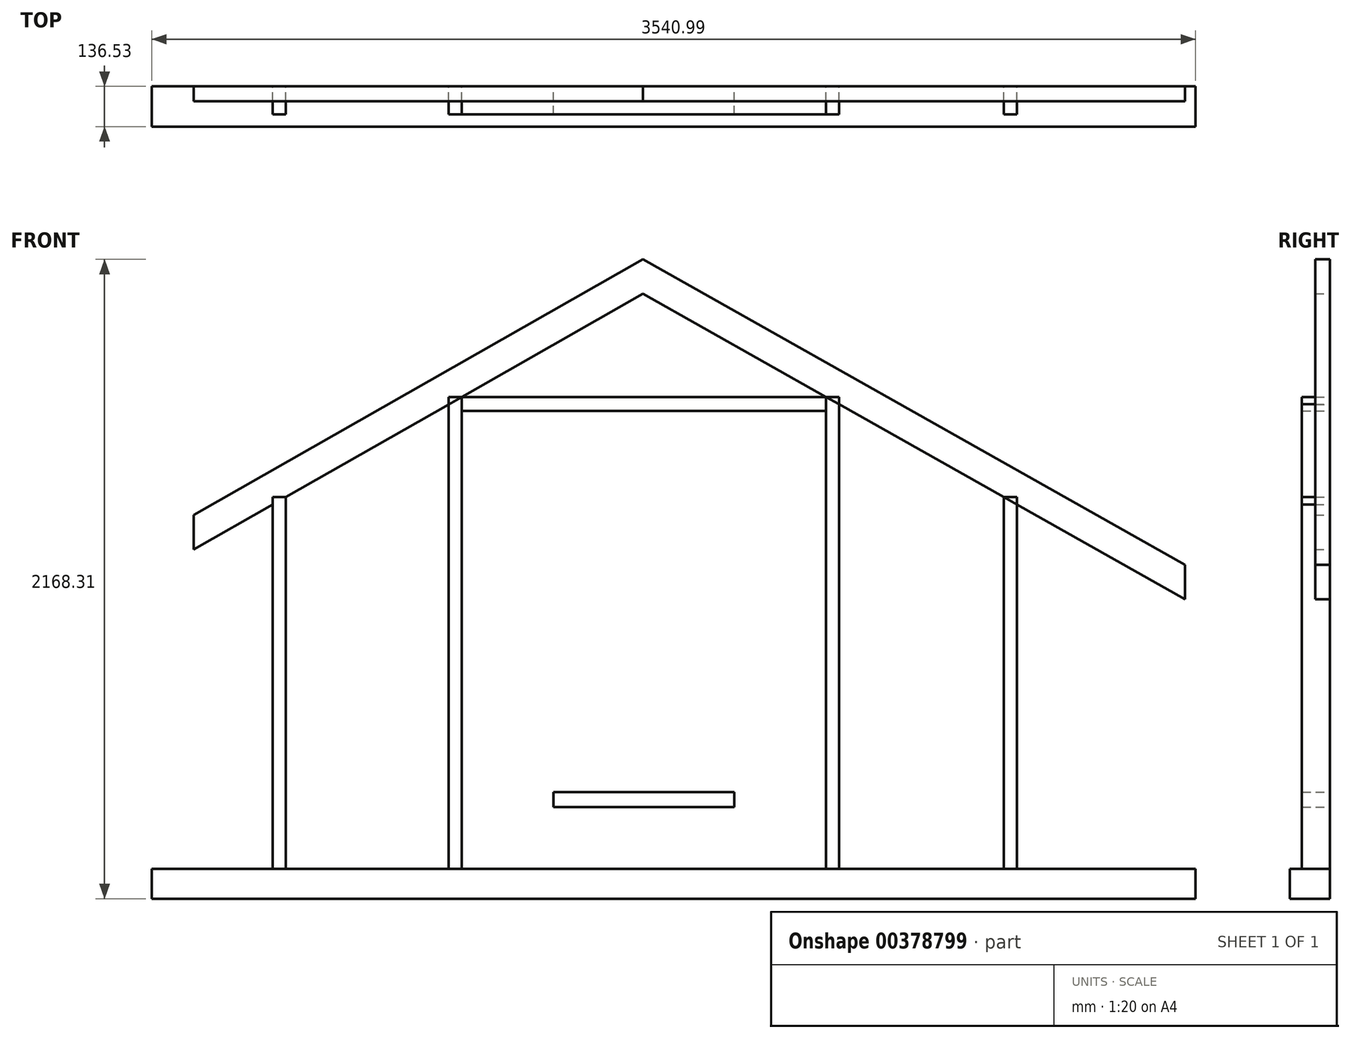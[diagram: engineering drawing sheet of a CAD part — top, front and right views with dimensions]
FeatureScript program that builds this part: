
annotation { "Feature Type Name" : "Feature", "Feature Type Description" : "" }
export const myFeature = defineFeature(function(context is Context, id is Id, definition is map)
    precondition{}
    {
        {
            var Q0;
            Q0=qCreatedBy(makeId("Front.planeOp"),FACE);
            var sketch = newSketch(context, id + "F0", { "sketchPlane" : qUnion([Q0])});
            skLineSegment(sketch, "E0.bottom", {"start": v(-586.63, -18.31) * mm, "end": v(648.44, -18.31) * mm});
            skLineSegment(sketch, "E0.top", {"start": v(-586.63, -65.94) * mm, "end": v(648.44, -65.94) * mm});
            skLineSegment(sketch, "E0.left", {"start": v(-586.63, -18.31) * mm, "end": v(-586.63, -65.94) * mm});
            skLineSegment(sketch, "E0.right", {"start": v(648.44, -18.31) * mm, "end": v(648.44, -65.94) * mm});
            skLineSegment(sketch, "E1.bottom", {"start": v(648.44, -18.31) * mm, "end": v(692.9, -18.31) * mm});
            skLineSegment(sketch, "E1.top", {"start": v(648.44, -1618.51) * mm, "end": v(692.9, -1618.51) * mm});
            skLineSegment(sketch, "E1.left", {"start": v(648.44, -18.31) * mm, "end": v(648.44, -1618.51) * mm});
            skLineSegment(sketch, "E1.right", {"start": v(692.9, -18.31) * mm, "end": v(692.9, -1618.51) * mm});
            skLineSegment(sketch, "E2.bottom", {"start": v(337.3, -65.94) * mm, "end": v(381.74, -65.94) * mm});
            skLineSegment(sketch, "E2.top", {"start": v(337.3, -1618.51) * mm, "end": v(381.74, -1618.51) * mm});
            skLineSegment(sketch, "E2.left", {"start": v(337.3, -65.94) * mm, "end": v(337.3, -1618.51) * mm});
            skLineSegment(sketch, "E2.right", {"start": v(381.74, -65.94) * mm, "end": v(381.74, -1618.51) * mm});
            skLineSegment(sketch, "E3.bottom", {"start": v(1251.7, -358.04) * mm, "end": v(1296.14, -358.04) * mm});
            skLineSegment(sketch, "E3.top", {"start": v(1251.7, -1618.51) * mm, "end": v(1296.14, -1618.51) * mm});
            skLineSegment(sketch, "E3.left", {"start": v(1251.7, -358.04) * mm, "end": v(1251.7, -1618.51) * mm});
            skLineSegment(sketch, "E3.right", {"start": v(1296.14, -358.04) * mm, "end": v(1296.14, -1618.51) * mm});
            skLineSegment(sketch, "E4", {"start": v(1251.7, -358.04) * mm, "end": v(648.44, -18.31) * mm});
            skLineSegment(sketch, "E5", {"start": v(648.44, -18.31) * mm, "end": v(27.64, 331.3) * mm});
            skLineSegment(sketch, "E6.bottom", {"start": v(-586.63, -18.31) * mm, "end": v(-631.08, -18.31) * mm});
            skLineSegment(sketch, "E6.top", {"start": v(-586.63, -1618.51) * mm, "end": v(-631.08, -1618.51) * mm});
            skLineSegment(sketch, "E6.left", {"start": v(-586.63, -18.31) * mm, "end": v(-586.63, -1618.51) * mm});
            skLineSegment(sketch, "E6.right", {"start": v(-631.08, -18.31) * mm, "end": v(-631.08, -1618.51) * mm});
            skLineSegment(sketch, "E7.bottom", {"start": v(-319.93, -65.94) * mm, "end": v(-275.48, -65.94) * mm});
            skLineSegment(sketch, "E7.top", {"start": v(-319.93, -1618.51) * mm, "end": v(-275.48, -1618.51) * mm});
            skLineSegment(sketch, "E7.left", {"start": v(-319.93, -65.94) * mm, "end": v(-319.93, -1618.51) * mm});
            skLineSegment(sketch, "E7.right", {"start": v(-275.48, -65.94) * mm, "end": v(-275.48, -1618.51) * mm});
            skLineSegment(sketch, "E8.bottom", {"start": v(-1227.98, -358.04) * mm, "end": v(-1183.53, -358.04) * mm});
            skLineSegment(sketch, "E8.top", {"start": v(-1227.98, -1618.51) * mm, "end": v(-1183.53, -1618.51) * mm});
            skLineSegment(sketch, "E8.left", {"start": v(-1227.98, -358.04) * mm, "end": v(-1227.98, -1618.51) * mm});
            skLineSegment(sketch, "E8.right", {"start": v(-1183.53, -358.04) * mm, "end": v(-1183.53, -1618.51) * mm});
            skLineSegment(sketch, "E9", {"start": v(-1183.53, -358.04) * mm, "end": v(-586.63, -18.31) * mm});
            skLineSegment(sketch, "E10", {"start": v(-586.63, -18.31) * mm, "end": v(27.64, 331.3) * mm});
            skLineSegment(sketch, "E11.bottom", {"start": v(-275.48, -1358.16) * mm, "end": v(337.3, -1358.16) * mm});
            skLineSegment(sketch, "E11.top", {"start": v(-275.48, -1408.96) * mm, "end": v(337.3, -1408.96) * mm});
            skLineSegment(sketch, "E11.left", {"start": v(-275.48, -1358.16) * mm, "end": v(-275.48, -1408.96) * mm});
            skLineSegment(sketch, "E11.right", {"start": v(337.3, -1358.16) * mm, "end": v(337.3, -1408.96) * mm});
            skLineSegment(sketch, "E12", {"start": v(27.64, 331.3) * mm, "end": v(27.64, 448.2) * mm});
            skLineSegment(sketch, "E13", {"start": v(27.64, 448.2) * mm, "end": v(-1496.57, -419.3) * mm});
            skLineSegment(sketch, "E14", {"start": v(-1496.57, -419.3) * mm, "end": v(-1496.57, -536.2) * mm});
            skLineSegment(sketch, "E15", {"start": v(-1496.57, -536.2) * mm, "end": v(-1183.53, -358.04) * mm});
            skLineSegment(sketch, "E16", {"start": v(27.64, 448.2) * mm, "end": v(1866.28, -587.24) * mm});
            skLineSegment(sketch, "E17", {"start": v(1866.28, -587.24) * mm, "end": v(1866.28, -704.15) * mm});
            skLineSegment(sketch, "E18", {"start": v(1866.28, -704.15) * mm, "end": v(1251.7, -358.04) * mm});
            skLineSegment(sketch, "E19.bottom", {"start": v(-1638.65, -1618.51) * mm, "end": v(1902.34, -1618.51) * mm});
            skLineSegment(sketch, "E19.top", {"start": v(-1638.65, -1720.11) * mm, "end": v(1902.34, -1720.11) * mm});
            skLineSegment(sketch, "E19.left", {"start": v(-1638.65, -1618.51) * mm, "end": v(-1638.65, -1720.11) * mm});
            skLineSegment(sketch, "E19.right", {"start": v(1902.34, -1618.51) * mm, "end": v(1902.34, -1720.11) * mm});
            skSolve(sketch);
        }
        {
            var Q0;
            {var subQ2=sQuery(id+"F0.wireOp",EDGE,"E6.bottom");Q0=makeQuery(id+"F0.imprint","IMPRINT",FACE,{"disambiguationData":[TD([[makeQuery(id+"F0.imprint","IMPRINT",EDGE,{"derivedFrom":subQ2}),-1.0]])]});}
            var Q1;
            {var subQ4=sQuery(id+"F0.wireOp",EDGE,"E1.bottom");Q1=makeQuery(id+"F0.imprint","IMPRINT",FACE,{"disambiguationData":[TD([[makeQuery(id+"F0.imprint","IMPRINT",EDGE,{"derivedFrom":subQ4}),1.0]])]});}
            extrude(context, id + "F1", {"entities" : qUnion([Q0, Q1]), "depth" : 50.8 * mm});
        }
        {
            var Q0;
            {var subQ7=sQuery(id+"F0.wireOp",EDGE,"E0.bottom");Q0=makeQuery(id+"F0.imprint","IMPRINT",FACE,{"disambiguationData":[TD([[makeQuery(id+"F0.imprint","IMPRINT",EDGE,{"derivedFrom":subQ7}),-1.0]])]});}
            extrude(context, id + "F2", {"entities" : qUnion([Q0]), "depth" : 95.25 * mm});
        }
        {
            var Q0;
            Q0=makeQuery(id+"F0.imprint","IMPRINT",FACE,{"disambiguationData":[TD([[makeQuery(id+"F0.imprint","IMPRINT",EDGE,{"derivedFrom":sQuery(id+"F0.wireOp",EDGE,"E11.bottom")}),-1.0]])]});
            extrude(context, id + "F3", {"entities" : qUnion([Q0]), "depth" : 95.25 * mm});
        }
        {
            var Q0;
            {var subQ3=sQuery(id+"F0.wireOp",EDGE,"E7.left");Q0=makeQuery(id+"F0.imprint","IMPRINT",FACE,{"disambiguationData":[TD([[makeQuery(id+"F0.imprint","IMPRINT",EDGE,{"derivedFrom":subQ3}),-1.0]])]});}
            extrude(context, id + "F4", {"entities" : qUnion([Q0]), "operationType" : NewBodyOperationType.REMOVE, "oppositeDirection" : true, "depth" : 25.4 * mm});
        }
        {
            var Q0;
            {var subQ5=sQuery(id+"F0.wireOp",EDGE,"E11.bottom");Q0=makeQuery(id+"F0.imprint","IMPRINT",FACE,{"disambiguationData":[TD([[makeQuery(id+"F0.imprint","IMPRINT",EDGE,{"derivedFrom":subQ5}),1.0]])]});}
            extrude(context, id + "F5", {"entities" : qUnion([Q0]), "operationType" : NewBodyOperationType.REMOVE, "oppositeDirection" : true, "depth" : 25.4 * mm});
        }
        {
            var Q0;
            {var subQ5=sQuery(id+"F0.wireOp",EDGE,"E8.right");Q0=makeQuery(id+"F0.imprint","IMPRINT",FACE,{"disambiguationData":[TD([[makeQuery(id+"F0.imprint","IMPRINT",EDGE,{"derivedFrom":subQ5}),-1.0]])]});}
            var Q1;
            {var subQ0=sQuery(id+"F0.wireOp",EDGE,"E8.bottom");Q1=makeQuery(id+"F0.imprint","IMPRINT",FACE,{"disambiguationData":[TD([[makeQuery(id+"F0.imprint","IMPRINT",EDGE,{"derivedFrom":subQ0}),-1.0]])]});}
            var Q2;
            {var subQ1=sQuery(id+"F0.wireOp",EDGE,"E6.left");var subQ7=makeQuery(id+"F0.imprint","INTERSECT",VERTEX,{"derivedFrom":[sQuery(id+"F0.wireOp",EDGE,"E0.top"),subQ1]});Q2=makeQuery(id+"F0.imprint","IMPRINT",FACE,{"disambiguationData":[TD([[makeQuery(id+"F0.imprint","IMPRINT",EDGE,{"disambiguationData":[TD([[subQ7,-1.0]])],"derivedFrom":subQ1}),-1.0]])]});}
            var Q3;
            {var subQ4=sQuery(id+"F0.wireOp",EDGE,"E7.bottom");Q3=makeQuery(id+"F0.imprint","IMPRINT",FACE,{"disambiguationData":[TD([[makeQuery(id+"F0.imprint","IMPRINT",EDGE,{"derivedFrom":subQ4}),-1.0]])]});}
            var Q4;
            {var subQ5=sQuery(id+"F0.wireOp",EDGE,"E2.bottom");Q4=makeQuery(id+"F0.imprint","IMPRINT",FACE,{"disambiguationData":[TD([[makeQuery(id+"F0.imprint","IMPRINT",EDGE,{"derivedFrom":subQ5}),-1.0]])]});}
            var Q5;
            {var subQ1=sQuery(id+"F0.wireOp",EDGE,"E1.left");var subQ7=makeQuery(id+"F0.imprint","INTERSECT",VERTEX,{"derivedFrom":[sQuery(id+"F0.wireOp",EDGE,"E0.top"),subQ1]});Q5=makeQuery(id+"F0.imprint","IMPRINT",FACE,{"disambiguationData":[TD([[makeQuery(id+"F0.imprint","IMPRINT",EDGE,{"disambiguationData":[TD([[subQ7,-1.0]])],"derivedFrom":subQ1}),1.0]])]});}
            var Q6;
            {var subQ0=sQuery(id+"F0.wireOp",EDGE,"E3.left");Q6=makeQuery(id+"F0.imprint","IMPRINT",FACE,{"disambiguationData":[TD([[makeQuery(id+"F0.imprint","IMPRINT",EDGE,{"derivedFrom":subQ0}),1.0]])]});}
            extrude(context, id + "F6", {"entities" : qUnion([Q0, Q1, Q2, Q3, Q4, Q5, Q6]), "depth" : 95.25 * mm});
        }
        {
            var Q0;
            Q0=makeQuery(id+"F0.imprint","IMPRINT",FACE,{"disambiguationData":[TD([[makeQuery(id+"F0.imprint","IMPRINT",EDGE,{"derivedFrom":sQuery(id+"F0.wireOp",EDGE,"E19.top")}),1.0]])]});
            extrude(context, id + "F7", {"entities" : qUnion([Q0]), "depth" : 136.53 * mm});
        }
        {
            var Q0;
            {var subQ0=sQuery(id+"F0.wireOp",EDGE,"E6.bottom");Q0=makeQuery(id+"F0.imprint","IMPRINT",FACE,{"disambiguationData":[TD([[makeQuery(id+"F0.imprint","IMPRINT",EDGE,{"derivedFrom":subQ0}),1.0]])]});}
            extrude(context, id + "F8", {"entities" : qUnion([Q0]), "depth" : 50.8 * mm});
        }
    });
